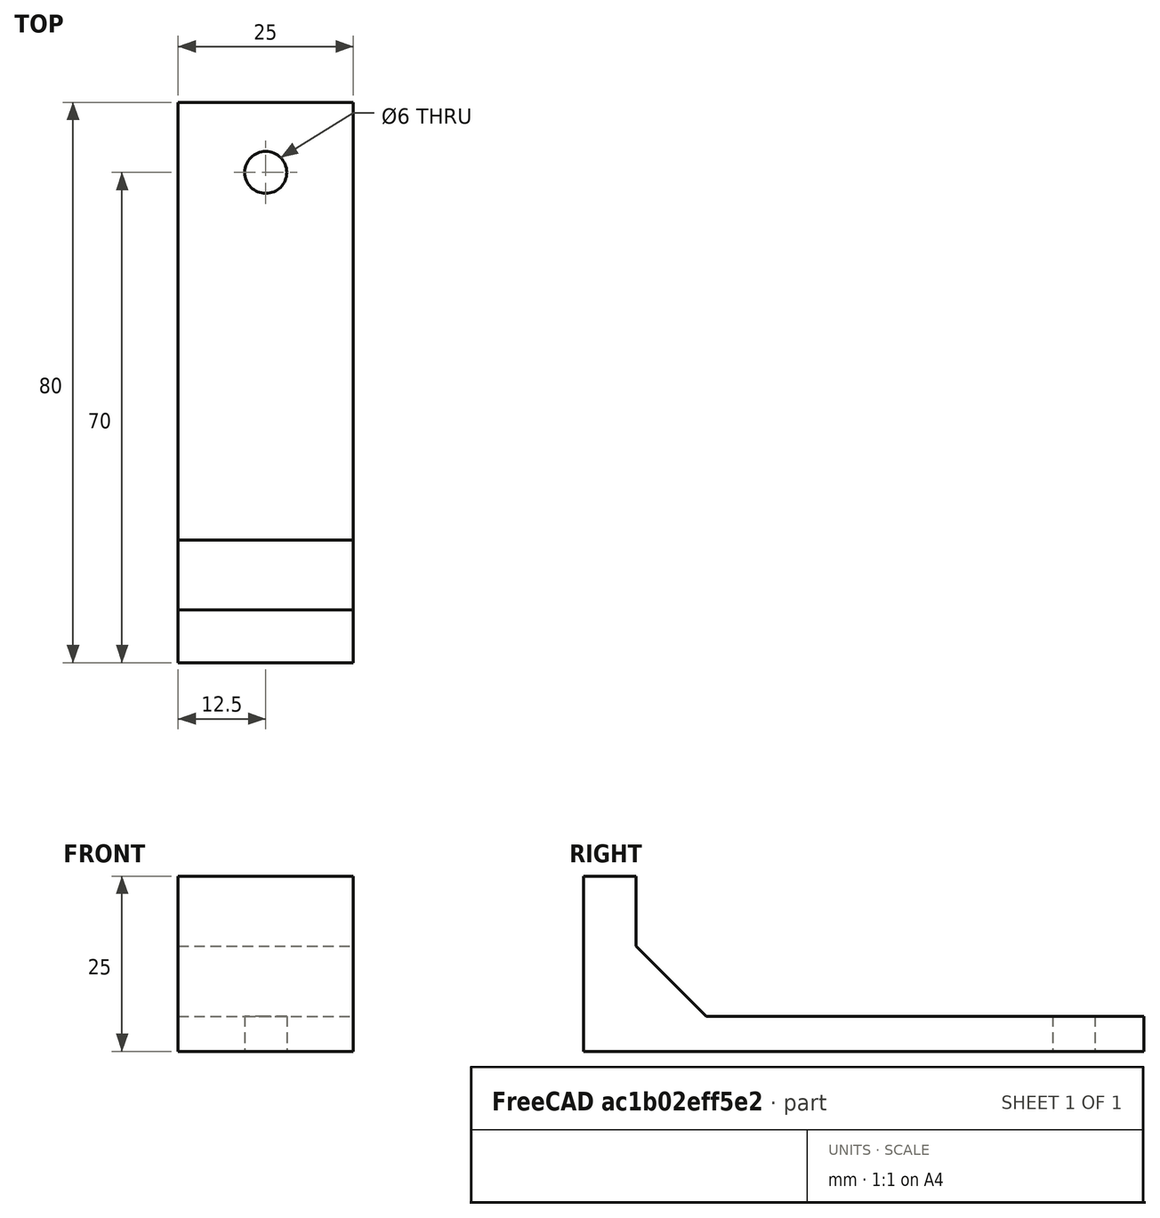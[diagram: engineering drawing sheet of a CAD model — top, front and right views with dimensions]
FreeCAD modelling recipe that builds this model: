
FCSTD DOCUMENT  (FreeCAD 0.18R4 (GitTag))
Label: headphone holder
License: All rights reserved
LicenseURL: http://en.wikipedia.org/wiki/All_rights_reserved
objects: Sketcher::SketchObject×2, App::MeasureDistance×2, PartDesign::Pad×1, PartDesign::Hole×1, PartDesign::Body×1
note: 7 computed .brp shape members not serialized (recipe doc carries the construction recipe); baked Part::Feature solids carry a one-line shape summary decoded from their .brp

FEATURE [Sketcher::SketchObject] CopySketch
  Placement = pos=(0,0,0) rot=(0.57735,0.57735,0.57735;2.0944rad)
  sketch-geometry (7):
    g0: LineSegment StartX=0 StartY=0 StartZ=0 EndX=0 EndY=25 EndZ=0
    g1: LineSegment StartX=0 StartY=0 StartZ=0 EndX=80 EndY=0 EndZ=0
    g2: LineSegment StartX=80 StartY=0 StartZ=0 EndX=80 EndY=5 EndZ=0
    g3: LineSegment StartX=80 StartY=5 StartZ=0 EndX=17.5 EndY=5 EndZ=0
    g4: LineSegment StartX=0 StartY=25 StartZ=0 EndX=7.5 EndY=25 EndZ=0
    g5: LineSegment StartX=7.5 StartY=25 StartZ=0 EndX=7.5 EndY=15 EndZ=0
    g6: LineSegment StartX=17.5 StartY=5 StartZ=0 EndX=7.5 EndY=15 EndZ=0
FEATURE [PartDesign::Pad] Pad
  Length = 25
  Length2 = 100
  Placement = pos=(0,0,0) rot=(0.57735,0.57735,0.57735;2.0944rad)
  Profile = -> CopySketch
  Type = 0
FEATURE [Sketcher::SketchObject] Sketch
  MapMode = 5
  Placement = pos=(-6e-16,0,5) rot=(0,0,-1;1.5708rad)
  Support = -> [Pad]
  sketch-geometry (1):
    g0: Circle CenterX=-70 CenterY=12.5 CenterZ=0 NormalX=0 NormalY=0 NormalZ=1 AngleXU=0 Radius=5
FEATURE [PartDesign::Hole] Hole
  Depth = 25
  DepthType = 1
  Diameter = 6
  DrillPoint = 1
  DrillPointAngle = 118
  HoleCutCountersinkAngle = 90
  HoleCutDepth = 0
  HoleCutDiameter = 0
  HoleCutType = 0
  ModelActualThread = false
  Placement = pos=(0,0,0) rot=(0.57735,0.57735,0.57735;2.0944rad)
  Profile = -> Sketch
  Tapered = false
  TaperedAngle = 90
  ThreadAngle = 0
  ThreadClass = 0
  ThreadCutOffInner = 0
  ThreadCutOffOuter = 0
  ThreadDirection = 0
  ThreadFit = 0
  ThreadPitch = 0
  ThreadSize = 0
  ThreadType = 0
  Threaded = false
FEATURE [PartDesign::Body] Body
  Group = -> [Hole]
  Origin = -> Origin
  Tip = -> Hole
FEATURE [App::MeasureDistance] Distance  label="Distance: 49.64 mm"
  Distance = 49.6413
  P1 = (13.2179,67.0872,5)
  P2 = (10.9001,17.5,5)
FEATURE [App::MeasureDistance] Distance001  label="Distance: 5.00 mm"
  Distance = 5.00015
  P1 = (2.23e-14,65.2152,5)
  P2 = (1.16e-14,65.1762,0)
